# Revit family: 1Electronics_Community_Biamp_Subwoofer_IS6-112WR
name_source: partatom
category: Communication Devices
units: mm (PartAtom-declared; Revit-internal decimal feet)

## family parameters
Cut with Voids When Loaded = No
Host = Face
Maintain Annotation Orientation = No
OmniClass Number = 23.85.10.11.14.14.14
OmniClass Title = Loudspeakers
Part Type = Normal
Room Calculation Point = No
Round Connector Dimension = Use Diameter
Shared = No

## types (3) — shared parameters
Continuous Power Handling  Nominal Impedance = Single Amp - 75V, 700W @ 8 ohms (2800W peak)
Default Elevation = 48 "
Depth = 21 "
Description = IS6-112WR Medium Power Single 12-Inch Weather-Resistant Subwoofer
Environmental = Outdoor: IP55W per IEC 60529 , MIL-STD-810G
Equalized Maximum SPL = Half Space - Peak: 130 dB - Continuous: 124 dB; Whole Space - Peak: 124 dB - Continuous: 118 dB
Equalized Sensitivity = Half Space - 1W: 96 dB - 2.83V: 96 dB; Whole Space - 1W: 90 dB - 2.83V: 90 dB
Height = 14.3 "
Input Connection = Screw terminal blocks (4-position)
Manufacturer = Biamp
Mounting Points = (22) M10 threaded rigging points
Nominal Maximum SPL = Half Space - Peak: 134 dB - Continuous: 128 dB; Whole Space - Peak: 128 dB - Continuous: 122 dB
Nominal Sensitivity = Half Space - 1W: 100 dB - 2.83V: 100 dB; Whole Space - 1W: 94 dB - 2.83V: 94 dB
Operating Environment = Weather-Resistant Outdoor
Operating Mode = Single Amp
Operating Range = 39 Hz to 150 Hz
Product Documentation Link = https://www.biamp.com
Product Page URL = https://www.biamp.com
Product data url = https://bimobject.com
Recommended Amplifiers = Single Amp - 700W - 1400W @ 8 ohms,  (75V - 106V)
Shipping Weight = 72.00 lbf
Transducers = 1 x 12 (305mm) double-treated cone with 4 (102mm) inner/outer wound voice coil, ferrite construction
URL = https://www.biamp.com
Weight = 64.00 lbf
Width = 14.5 "

## per-type parameters (varying)
| type | Grill Material | Housing Material |
| IS6-112WR B | Biamp - Plastic - Black(Grid) | Biamp - Plastic - Black |
| IS6-112WR W | Biamp - Plastic - White(Grid) | Biamp - Plastic - White |
| ІS6-112WR G | Biamp - Plastic - Gray(Grid) | Biamp - Plastic - Gray |

note: column(s) folded — value = type name in every type: Model

## geometry (parser evidence)
native form markers: Sweep x1
no freeform markers — native parametric forms only
